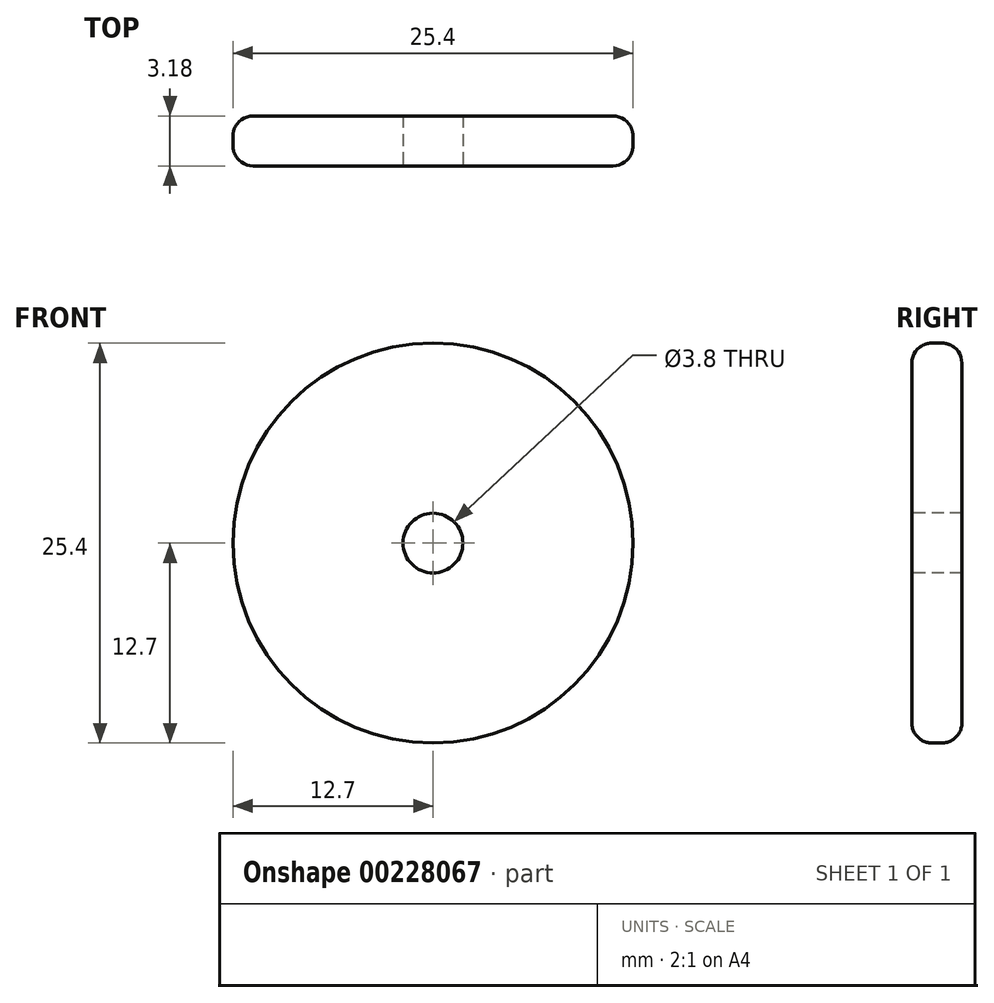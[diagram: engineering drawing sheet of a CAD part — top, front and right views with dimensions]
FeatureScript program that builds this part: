
annotation { "Feature Type Name" : "Feature", "Feature Type Description" : "" }
export const myFeature = defineFeature(function(context is Context, id is Id, definition is map)
    precondition{}
    {
        {
            var Q0;
            Q0=qCreatedBy(makeId("Front.planeOp"),FACE);
            var sketch = newSketch(context, id + "F0", { "sketchPlane" : qUnion([Q0])});
            skCircle(sketch, "E0", {"center": v(0, 0) * mm, "radius": 12.7 * mm});
            skSolve(sketch);
        }
        {
            var Q0;
            Q0 = qSketchRegion(id + "F0", true);
            extrude(context, id + "F1", {"entities" : qUnion([Q0]), "depth" : 3.17 * mm});
        }
        {
            var Q0;
            Q0=makeQuery(id+"F1.opExtrude","CAP_FACE",FACE,{"disambiguationData":[OSD([sQuery(id+"F0.wireOp",EDGE,"E0")])],"isStart":false});
            var sketch = newSketch(context, id + "F2", { "sketchPlane" : qUnion([Q0])});
            skPoint(sketch, "E1", {"position": v(0, 0) * mm});
            skSolve(sketch);
        }
        {
            var Q0;
            Q0=sQuery(id+"F2.wireOp",VERTEX,"E1");
            var Q1;
            Q1=makeQuery(id+"F1.opExtrude","SWEPT_BODY",BODY,{"disambiguationData":[OSD([sQuery(id+"F0.wireOp",EDGE,"E0")])]});
            hole(context, id + "F3", {"style" : HoleStyle.SIMPLE, "endStyle" : HoleEndStyle.THROUGH, "standardTappedOrClearance" : lookupTablePath({ "standard" : "ANSI", "fit" : "Normal (ASME)", "size" : "#6", "type" : "Clearance" }), "standardBlindInLast" : lookupTablePath({ "fit" : "Free", "standard" : "ANSI", "size" : "#6", "type" : "Clearance" }), "holeDiameter" : 3.8 * mm, "locations" : qUnion([Q0]), "scope" : qUnion([Q1]), "isTappedThrough" : true});
        }
        {
            var Q0;
            Q0=makeQuery(id+"F1.opExtrude","CAP_EDGE",EDGE,{"disambiguationData":[OSD([sQuery(id+"F0.wireOp",EDGE,"E0")])],"isStart":false});
            var Q1;
            Q1=makeQuery(id+"F1.opExtrude","CAP_EDGE",EDGE,{"disambiguationData":[OSD([sQuery(id+"F0.wireOp",EDGE,"E0")])],"isStart":true});
            fillet(context, id + "F4", {"entities" : qUnion([Q0, Q1]), "radius" : 1.27 * mm, "tangentPropagation" : true, "allowEdgeOverflow" : false});
        }
    });
